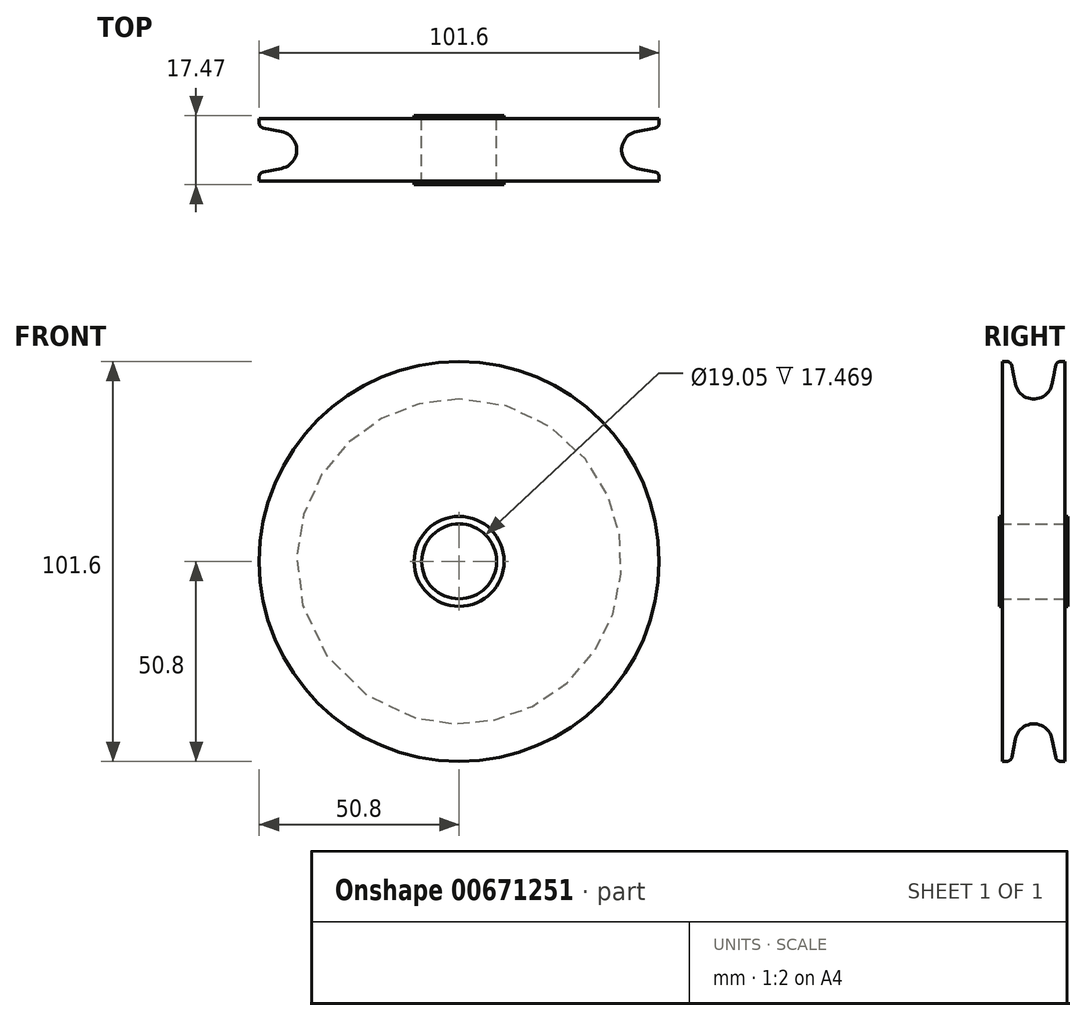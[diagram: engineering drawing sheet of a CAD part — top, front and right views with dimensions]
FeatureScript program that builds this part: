
annotation { "Feature Type Name" : "Feature", "Feature Type Description" : "" }
export const myFeature = defineFeature(function(context is Context, id is Id, definition is map)
    precondition{}
    {
        {
            var Q0;
            Q0=qCreatedBy(makeId("Front.planeOp"),FACE);
            var sketch = newSketch(context, id + "F0", { "sketchPlane" : qUnion([Q0])});
            skCircle(sketch, "E0", {"center": v(0, 0) * mm, "radius": 9.53 * mm});
            skCircle(sketch, "E1", {"center": v(0, 0) * mm, "radius": 50.8 * mm});
            skCircle(sketch, "E2", {"center": v(0, 0) * mm, "radius": 11.43 * mm});
            skSolve(sketch);
        }
        {
            var Q0;
            Q0=makeQuery(id+"F0.imprint","IMPRINT",FACE,{"disambiguationData":[TD([[makeQuery(id+"F0.imprint","IMPRINT",EDGE,{"derivedFrom":sQuery(id+"F0.wireOp",EDGE,"E0")}),-1.0]])]});
            extrude(context, id + "F1", {"entities" : qUnion([Q0]), "depth" : 8.73 * mm, "offsetDistance" : 25.4 * mm, "hasSecondDirection" : true, "secondDirectionOppositeDirection" : true, "secondDirectionDepth" : 8.74 * mm});
        }
        {
            var Q0;
            Q0 = qSketchRegion(id + "F0", true);
            extrude(context, id + "F2", {"entities" : qUnion([Q0]), "operationType" : NewBodyOperationType.ADD, "depth" : 7.94 * mm, "offsetDistance" : 25.4 * mm, "hasSecondDirection" : true, "secondDirectionOppositeDirection" : true, "secondDirectionDepth" : 7.95 * mm});
        }
        {
            var Q0;
            Q0=qCreatedBy(makeId("Right.planeOp"),FACE);
            var sketch = newSketch(context, id + "F3", { "sketchPlane" : qUnion([Q0])});
            skArc(sketch, "E3", {"start": v(-4.67, 45.12) * mm, "mid": v(0, 41.27) * mm, "end": v(4.67, 45.12) * mm});
            skLineSegment(sketch, "E4", {"start": v(-6.35, 53.66) * mm, "end": v(6.35, 53.66) * mm});
            skLineSegment(sketch, "E5", {"start": v(0, 46.04) * mm, "end": v(0, 53.66) * mm});
            skLineSegment(sketch, "E6", {"start": v(6.35, 53.66) * mm, "end": v(4.67, 45.12) * mm});
            skLineSegment(sketch, "E7", {"start": v(-6.35, 53.66) * mm, "end": v(-4.67, 45.12) * mm});
            skLineSegment(sketch, "E8", {"start": v(0, 0) * mm, "end": v(67.78, 0) * mm});
            skSolve(sketch);
        }
        {
            var Q0;
            Q0=makeQuery(id+"F3.imprint","IMPRINT",FACE,{"disambiguationData":[TD([[makeQuery(id+"F3.imprint","IMPRINT",EDGE,{"derivedFrom":sQuery(id+"F3.wireOp",EDGE,"E3")}),1.0]])]});
            var Q1;
            Q1=sQuery(id+"F3.wireOp",EDGE,"E8");
            revolve(context, id + "F4", {"operationType" : NewBodyOperationType.REMOVE, "surfaceOperationType" : NewSurfaceOperationType.NEW, "entities" : qUnion([Q0]), "axis" : qUnion([Q1]), "revolveType" : RevolveType.FULL, "oppositeDirection" : true});
        }
        {
            var Q0;
            Q0=makeQuery(id+"F4.boolean.opBoolean","INTERSECT",EDGE,{"derivedFrom":[makeQuery(id+"F2.opExtrude","SWEPT_FACE",FACE,{"disambiguationData":[OSD([sQuery(id+"F0.wireOp",EDGE,"E1")])]}),makeQuery(id+"F4.opRevolve","SWEPT_FACE",FACE,{"disambiguationData":[OSD([sQuery(id+"F3.wireOp",EDGE,"E7")])]})]});
            var Q1;
            Q1=makeQuery(id+"F4.boolean.opBoolean","INTERSECT",EDGE,{"derivedFrom":[makeQuery(id+"F2.opExtrude","SWEPT_FACE",FACE,{"disambiguationData":[OSD([sQuery(id+"F0.wireOp",EDGE,"E1")])]}),makeQuery(id+"F4.opRevolve","SWEPT_FACE",FACE,{"disambiguationData":[OSD([sQuery(id+"F3.wireOp",EDGE,"E6")])]})]});
            fillet(context, id + "F5", {"entities" : qUnion([Q0, Q1]), "radius" : 1.27 * mm, "tangentPropagation" : true, "allowEdgeOverflow" : false});
        }
    });
